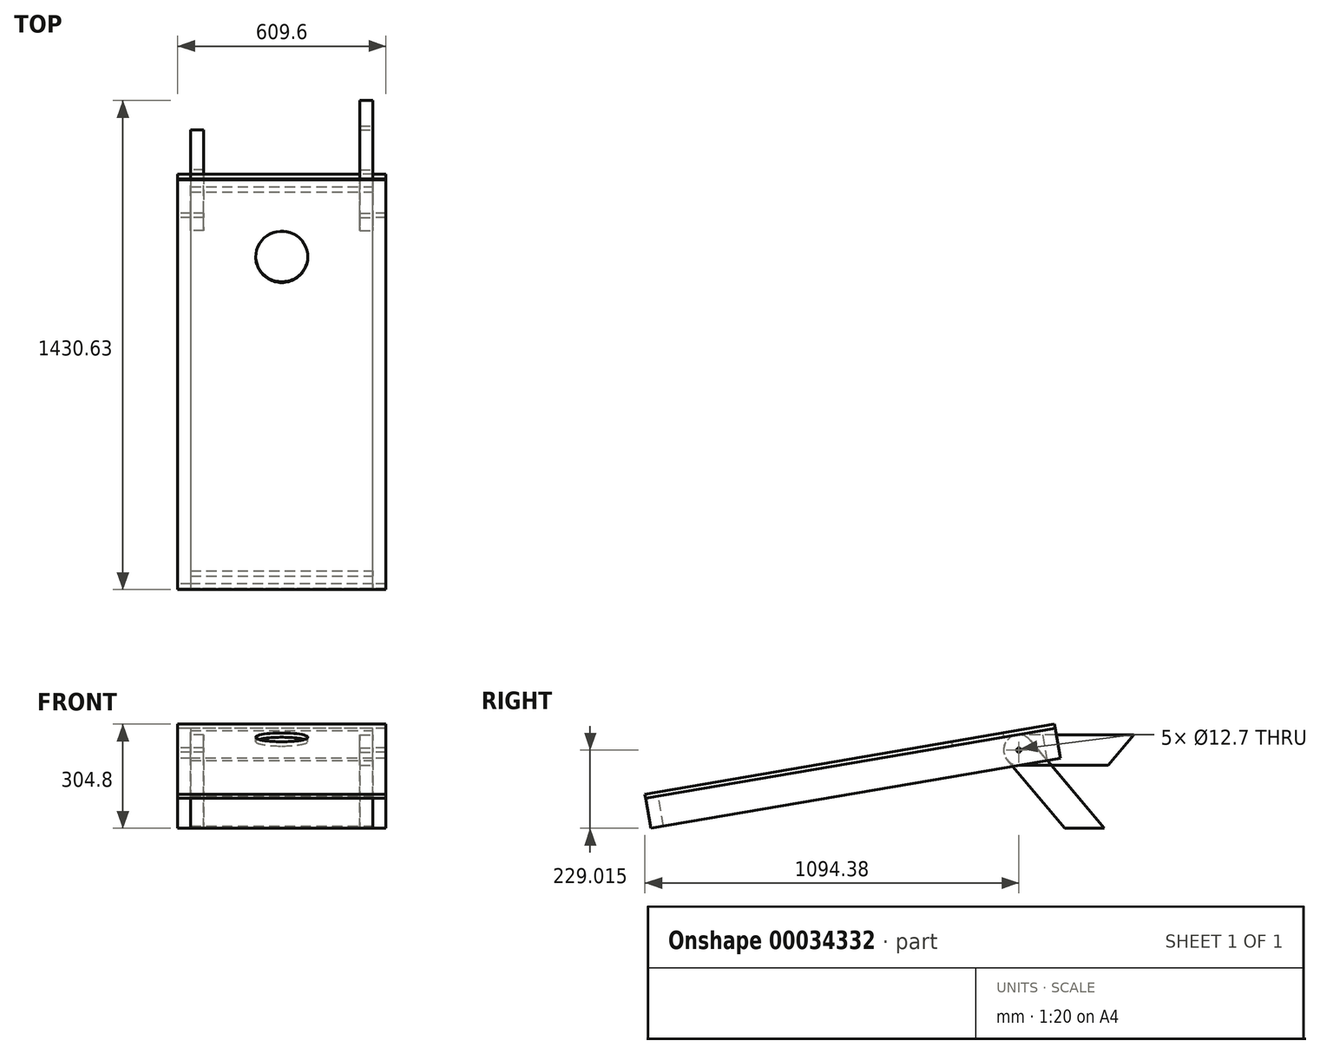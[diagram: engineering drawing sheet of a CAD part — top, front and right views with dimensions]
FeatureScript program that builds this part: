
annotation { "Feature Type Name" : "Feature", "Feature Type Description" : "" }
export const myFeature = defineFeature(function(context is Context, id is Id, definition is map)
    precondition{}
    {
        {
            var Q0;
            Q0=qCreatedBy(makeId("Right.planeOp"),FACE);
            var sketch = newSketch(context, id + "F0", { "sketchPlane" : qUnion([Q0])});
            skLineSegment(sketch, "E0", {"start": v(-37.56, 0) * mm, "end": v(-52.52, 87.63) * mm, "construction": true});
            skLineSegment(sketch, "E1", {"start": v(-52.52, 87.63) * mm, "end": v(-14.96, 94.04) * mm, "construction": true});
            skLineSegment(sketch, "E2", {"start": v(-14.96, 94.04) * mm, "end": v(0, 6.41) * mm, "construction": true});
            skLineSegment(sketch, "E3", {"start": v(0, 6.41) * mm, "end": v(-37.56, 0) * mm, "construction": true});
            skLineSegment(sketch, "E4", {"start": v(0, 0) * mm, "end": v(-37.56, 0) * mm, "construction": true});
            skLineSegment(sketch, "E5", {"start": v(-52.52, 87.63) * mm, "end": v(1146.16, 292.28) * mm});
            skLineSegment(sketch, "E6", {"start": v(1146.16, 292.28) * mm, "end": v(1144.03, 304.8) * mm});
            skLineSegment(sketch, "E7", {"start": v(1144.03, 304.8) * mm, "end": v(-54.66, 100.15) * mm});
            skLineSegment(sketch, "E8", {"start": v(-54.66, 100.15) * mm, "end": v(-52.52, 87.63) * mm});
            skLineSegment(sketch, "E9", {"start": v(0, 6.41) * mm, "end": v(0, 0) * mm, "construction": true});
            skSolve(sketch);
        }
        {
            var Q0;
            Q0 = qSketchRegion(id + "F0", true);
            extrude(context, id + "F1", {"entities" : qUnion([Q0]), "endBound" : BoundingType.SYMMETRIC, "depth" : 609.6 * mm});
        }
        {
            var Q0;
            Q0=makeQuery(id+"F1.opExtrude","SWEPT_FACE",FACE,{"disambiguationData":[OSD([sQuery(id+"F0.wireOp",EDGE,"E5")])]});
            var sketch = newSketch(context, id + "F2", { "sketchPlane" : qUnion([Q0])});
            skLineSegment(sketch, "E10.bottom", {"start": v(-304.8, 37.02) * mm, "end": v(-266.7, 37.02) * mm});
            skLineSegment(sketch, "E10.top", {"start": v(-304.8, -1179) * mm, "end": v(-266.7, -1179) * mm});
            skLineSegment(sketch, "E10.left", {"start": v(-304.8, -1179) * mm, "end": v(-304.8, 37.02) * mm});
            skLineSegment(sketch, "E10.right", {"start": v(-266.7, -1179) * mm, "end": v(-266.7, 37.02) * mm});
            skLineSegment(sketch, "E11.bottom", {"start": v(304.8, -1179) * mm, "end": v(266.7, -1179) * mm});
            skLineSegment(sketch, "E11.top", {"start": v(304.8, 37.02) * mm, "end": v(266.7, 37.02) * mm});
            skLineSegment(sketch, "E11.left", {"start": v(304.8, 37.02) * mm, "end": v(304.8, -1179) * mm});
            skLineSegment(sketch, "E11.right", {"start": v(266.7, 37.02) * mm, "end": v(266.7, -1179) * mm});
            skLineSegment(sketch, "E12.bottom", {"start": v(-266.7, 37.02) * mm, "end": v(266.7, 37.02) * mm});
            skLineSegment(sketch, "E12.top", {"start": v(-266.7, -1.08) * mm, "end": v(266.7, -1.08) * mm});
            skLineSegment(sketch, "E12.left", {"start": v(-266.7, 37.02) * mm, "end": v(-266.7, -1.08) * mm});
            skLineSegment(sketch, "E12.right", {"start": v(266.7, 37.02) * mm, "end": v(266.7, -1.08) * mm});
            skLineSegment(sketch, "E13.bottom", {"start": v(-266.7, -1179) * mm, "end": v(266.7, -1179) * mm});
            skLineSegment(sketch, "E13.top", {"start": v(-266.7, -1140.9) * mm, "end": v(266.7, -1140.9) * mm});
            skLineSegment(sketch, "E13.left", {"start": v(-266.7, -1179) * mm, "end": v(-266.7, -1140.9) * mm});
            skLineSegment(sketch, "E13.right", {"start": v(266.7, -1179) * mm, "end": v(266.7, -1140.9) * mm});
            skSolve(sketch);
        }
        {
            var Q0;
            Q0=makeQuery(id+"F2.imprint","IMPRINT",FACE,{"disambiguationData":[TD([[makeQuery(id+"F2.imprint","IMPRINT",EDGE,{"derivedFrom":sQuery(id+"F2.wireOp",EDGE,"E12.bottom")}),1.0]])]});
            var Q1;
            Q1=makeQuery(id+"F2.imprint","IMPRINT",FACE,{"disambiguationData":[TD([[makeQuery(id+"F2.imprint","IMPRINT",EDGE,{"derivedFrom":sQuery(id+"F2.wireOp",EDGE,"E13.bottom")}),-1.0]])]});
            extrude(context, id + "F3", {"entities" : qUnion([Q0, Q1]), "depth" : 88.9 * mm});
        }
        {
            var Q0;
            Q0=makeQuery(id+"F2.imprint","IMPRINT",FACE,{"disambiguationData":[TD([[makeQuery(id+"F2.imprint","IMPRINT",EDGE,{"derivedFrom":sQuery(id+"F2.wireOp",EDGE,"E10.bottom")}),1.0]])]});
            var Q1;
            Q1=makeQuery(id+"F2.imprint","IMPRINT",FACE,{"disambiguationData":[TD([[makeQuery(id+"F2.imprint","IMPRINT",EDGE,{"derivedFrom":sQuery(id+"F2.wireOp",EDGE,"E11.bottom")}),-1.0]])]});
            var Q2;
            Q2=makeQuery(id+"F3.opExtrude","CAP_FACE",FACE,{"disambiguationData":[OSD([sQuery(id+"F2.wireOp",EDGE,"E12.bottom"),sQuery(id+"F2.wireOp",EDGE,"E12.top"),sQuery(id+"F2.wireOp",EDGE,"E12.left"),sQuery(id+"F2.wireOp",EDGE,"E12.right")])],"isStart":false});
            extrude(context, id + "F4", {"entities" : qUnion([Q0, Q1]), "endBound" : BoundingType.UP_TO_SURFACE, "endBoundEntityFace" : qUnion([Q2]), "depth" : 25.4 * mm});
        }
        {
            var Q0;
            Q0=makeQuery(id+"F1.opExtrude","SWEPT_FACE",FACE,{"disambiguationData":[OSD([sQuery(id+"F0.wireOp",EDGE,"E7")])]});
            var sketch = newSketch(context, id + "F5", { "sketchPlane" : qUnion([Q0])});
            skCircle(sketch, "E14", {"center": v(0, 950.4) * mm, "radius": 76.2 * mm});
            skLineSegment(sketch, "E15", {"start": v(0, 1179) * mm, "end": v(0, 950.4) * mm, "construction": true});
            skSolve(sketch);
        }
        {
            var Q0;
            Q0=makeQuery(id+"F5.imprint","IMPRINT",FACE,{"disambiguationData":[TD([[makeQuery(id+"F5.imprint","IMPRINT",EDGE,{"derivedFrom":sQuery(id+"F5.wireOp",EDGE,"E14")}),1.0]])]});
            extrude(context, id + "F6", {"entities" : qUnion([Q0]), "operationType" : NewBodyOperationType.REMOVE, "endBound" : BoundingType.THROUGH_ALL, "oppositeDirection" : true, "depth" : 25.4 * mm});
        }
        {
            var Q0;
            Q0=makeQuery(id+"F4.opExtrude","SWEPT_FACE",FACE,{"disambiguationData":[OSD([sQuery(id+"F2.wireOp",EDGE,"E11.right"),sQuery(id+"F2.wireOp",EDGE,"E12.right"),sQuery(id+"F2.wireOp",EDGE,"E13.right")])]});
            var sketch = newSketch(context, id + "F7", { "sketchPlane" : qUnion([Q0])});
            skLineSegment(sketch, "E16", {"start": v(37.56, 0) * mm, "end": v(-1173.86, 0) * mm, "construction": true});
            skCircle(sketch, "E17", {"center": v(-1039.72, 229.01) * mm, "radius": 6.35 * mm});
            skArc(sketch, "E18", {"start": v(-1005.67, 200.44) * mm, "mid": v(-1011.14, 263.07) * mm, "end": v(-1073.77, 257.59) * mm});
            skLineSegment(sketch, "E19", {"start": v(-1005.67, 200.44) * mm, "end": v(-1173.86, 0) * mm});
            skLineSegment(sketch, "E20", {"start": v(-1173.86, 0) * mm, "end": v(-1289.9, 0) * mm});
            skLineSegment(sketch, "E21", {"start": v(-1289.9, 0) * mm, "end": v(-1073.77, 257.59) * mm});
            skLineSegment(sketch, "E22", {"start": v(-1153.64, 248.47) * mm, "end": v(-1039.72, 229.01) * mm, "construction": true});
            skSolve(sketch);
        }
        {
            var Q0;
            Q0 = qSketchRegion(id + "F7", true);
            extrude(context, id + "F8", {"entities" : qUnion([Q0]), "depth" : 38.1 * mm});
        }
        {
            var Q0;
            Q0=makeQuery(id+"F8.opExtrude","SWEPT_BODY",BODY,{"disambiguationData":[OSD([sQuery(id+"F7.wireOp",EDGE,"E17"),sQuery(id+"F7.wireOp",EDGE,"E18"),sQuery(id+"F7.wireOp",EDGE,"E19"),sQuery(id+"F7.wireOp",EDGE,"E20"),sQuery(id+"F7.wireOp",EDGE,"E21")])]});
            var Q1;
            Q1=qCreatedBy(makeId("Right.planeOp"),FACE);
            mirror(context, id + "F9", {"entities" : qUnion([Q0]), "mirrorPlane" : qUnion([Q1])});
        }
        {
            var Q0;
            Q0=makeQuery(id+"F7.imprint","IMPRINT",FACE,{"disambiguationData":[TD([[makeQuery(id+"F7.imprint","IMPRINT",EDGE,{"derivedFrom":sQuery(id+"F7.wireOp",EDGE,"E17")}),1.0]])]});
            extrude(context, id + "F10", {"entities" : qUnion([Q0]), "operationType" : NewBodyOperationType.REMOVE, "endBound" : BoundingType.THROUGH_ALL, "oppositeDirection" : true, "depth" : 25.4 * mm, "hasSecondDirection" : true, "secondDirectionBound" : SecondDirectionBoundingType.THROUGH_ALL, "secondDirectionOppositeDirection" : false, "secondDirectionDepth" : 25.4 * mm});
        }
        {
            var Q0;
            Q0=makeQuery(id+"F8.opExtrude","SWEPT_BODY",BODY,{"disambiguationData":[OSD([sQuery(id+"F7.wireOp",EDGE,"E17"),sQuery(id+"F7.wireOp",EDGE,"E18"),sQuery(id+"F7.wireOp",EDGE,"E19"),sQuery(id+"F7.wireOp",EDGE,"E20"),sQuery(id+"F7.wireOp",EDGE,"E21")])]});
            var Q1;
            Q1=makeQuery(id+"F10.boolean.opBoolean","INTERSECT",EDGE,{"derivedFrom":[makeQuery(id+"F4.opExtrude","SWEPT_FACE",FACE,{"disambiguationData":[OSD([sQuery(id+"F2.wireOp",EDGE,"E11.left")])]}),makeQuery(id+"F10.opExtrude","SWEPT_FACE",FACE,{"disambiguationData":[OSD([sQuery(id+"F7.wireOp",EDGE,"E17")])]})]});
            circularPattern(context, id + "F11", {"entities" : qUnion([Q0]), "axis" : qUnion([Q1]), "angle" : 50 * degree, "instanceCount" : 2});
        }
    });
